# Revit family: CITY ALPHABET letter „H”
name_source: partatom
category: Furniture
revit_build: Autodesk Revit 2018 (Build: 20190510_1515(x64)
units: mm (PartAtom-declared; Revit-internal decimal feet)

## family parameters
Cut with Voids When Loaded = No
Host = Face
OmniClass Number = 23.40.10.11.14
OmniClass Title = Exterior Seating
Room Calculation Point = No
Shared = No

## types (1)
- CITY ALPHABET letter „H”
    Default Elevation = 1219 mm
    Height = 590 mm  [stored 1.9357 ft]
    IfcExportAs = IfcFurnishingElement
    Length = 3250 mm  [stored 10.6627 ft]
    Manufacturer = Astrini Design
    Material information = Colour choice from RAL colour standard. Customer may inquire about specific request regarding individual order.
    Model = CITY ALPHABET letter „H”
    Operating temperature = -40°C to 80°C, ( -40°F to 176°F )
    Type Comments = Bench
    Type Image = H.jpg
    URL = https://astrini-design.pl
    Weight (approximately) = 69.40 kg
    Weight - filled (approximately) = 169.00 kg
    Width = 1650 mm  [stored 5.41339 ft]

note: [stored X ft] marks values corroborated as IEEE doubles in the binary element streams (Revit-internal decimal feet)
